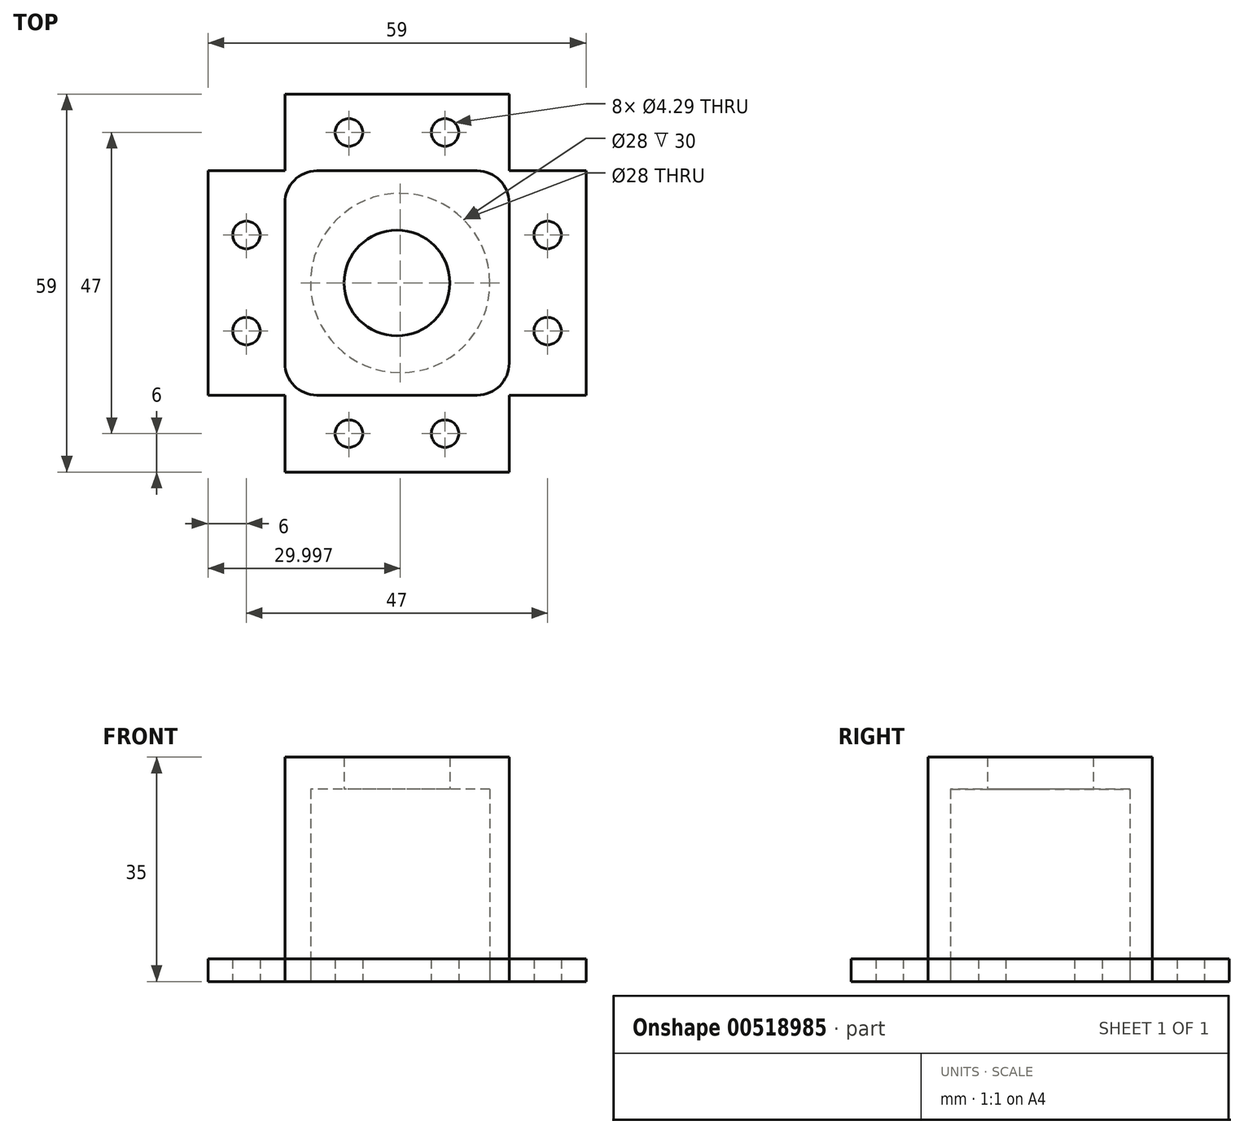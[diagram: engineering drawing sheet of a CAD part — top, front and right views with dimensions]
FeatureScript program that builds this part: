
annotation { "Feature Type Name" : "Feature", "Feature Type Description" : "" }
export const myFeature = defineFeature(function(context is Context, id is Id, definition is map)
    precondition{}
    {
        {
            var Q0;
            Q0=qCreatedBy(makeId("Top.planeOp"),FACE);
            var sketch = newSketch(context, id + "F0", { "sketchPlane" : qUnion([Q0])});
            skLineSegment(sketch, "E0.bottom", {"start": v(-17.5, 17.5) * mm, "end": v(17.5, 17.5) * mm});
            skLineSegment(sketch, "E0.top", {"start": v(-17.5, -17.5) * mm, "end": v(17.5, -17.5) * mm});
            skLineSegment(sketch, "E0.left", {"start": v(-17.5, 17.5) * mm, "end": v(-17.5, -17.5) * mm});
            skLineSegment(sketch, "E0.right", {"start": v(17.5, 17.5) * mm, "end": v(17.5, -17.5) * mm});
            skLineSegment(sketch, "E1.bottom", {"start": v(-17.5, 17.5) * mm, "end": v(-29.5, 17.5) * mm});
            skLineSegment(sketch, "E1.top", {"start": v(-17.5, -17.5) * mm, "end": v(-29.5, -17.5) * mm});
            skLineSegment(sketch, "E1.right", {"start": v(-29.5, 17.5) * mm, "end": v(-29.5, -17.5) * mm});
            skLineSegment(sketch, "E2.left", {"start": v(-17.5, 17.5) * mm, "end": v(-17.5, 17.5) * mm});
            skLineSegment(sketch, "E2.right", {"start": v(17.5, 17.5) * mm, "end": v(17.5, 17.5) * mm});
            skLineSegment(sketch, "E3.top", {"start": v(-17.5, 29.5) * mm, "end": v(17.5, 29.5) * mm});
            skLineSegment(sketch, "E3.left", {"start": v(-17.5, 17.5) * mm, "end": v(-17.5, 29.5) * mm});
            skLineSegment(sketch, "E3.right", {"start": v(17.5, 17.5) * mm, "end": v(17.5, 29.5) * mm});
            skLineSegment(sketch, "E4.bottom", {"start": v(17.5, 17.5) * mm, "end": v(29.5, 17.5) * mm});
            skLineSegment(sketch, "E4.top", {"start": v(17.5, -17.5) * mm, "end": v(29.5, -17.5) * mm});
            skLineSegment(sketch, "E4.right", {"start": v(29.5, 17.5) * mm, "end": v(29.5, -17.5) * mm});
            skLineSegment(sketch, "E5.top", {"start": v(-17.5, -29.5) * mm, "end": v(17.5, -29.5) * mm});
            skLineSegment(sketch, "E5.left", {"start": v(-17.5, -17.5) * mm, "end": v(-17.5, -29.5) * mm});
            skLineSegment(sketch, "E5.right", {"start": v(17.5, -17.5) * mm, "end": v(17.5, -29.5) * mm});
            skLineSegment(sketch, "E6", {"start": v(17.5, 17.5) * mm, "end": v(-17.5, -17.5) * mm, "construction": true});
            skLineSegment(sketch, "E7", {"start": v(-17.5, 17.5) * mm, "end": v(17.5, -17.5) * mm, "construction": true});
            skCircle(sketch, "E8", {"center": v(0, 0) * mm, "radius": 8.25 * mm});
            skCircle(sketch, "E9", {"center": v(-23.5, 7.5) * mm, "radius": 2.14 * mm});
            skCircle(sketch, "E10", {"center": v(-23.5, -7.5) * mm, "radius": 2.14 * mm});
            skCircle(sketch, "E11", {"center": v(23.5, -7.5) * mm, "radius": 2.14 * mm});
            skCircle(sketch, "E12", {"center": v(23.5, 7.5) * mm, "radius": 2.14 * mm});
            skCircle(sketch, "E13", {"center": v(-7.5, 23.5) * mm, "radius": 2.14 * mm});
            skCircle(sketch, "E14", {"center": v(7.5, 23.5) * mm, "radius": 2.14 * mm});
            skCircle(sketch, "E15", {"center": v(-7.5, -23.5) * mm, "radius": 2.14 * mm});
            skCircle(sketch, "E16", {"center": v(7.5, -23.5) * mm, "radius": 2.14 * mm});
            skLineSegment(sketch, "E17", {"start": v(-23.5, 7.5) * mm, "end": v(-29.5, 7.5) * mm, "construction": true});
            skLineSegment(sketch, "E18", {"start": v(-23.5, 7.5) * mm, "end": v(-17.5, 7.5) * mm, "construction": true});
            skLineSegment(sketch, "E19", {"start": v(23.5, -7.5) * mm, "end": v(29.5, -7.5) * mm, "construction": true});
            skLineSegment(sketch, "E20", {"start": v(23.5, -7.5) * mm, "end": v(17.5, -7.5) * mm, "construction": true});
            skLineSegment(sketch, "E21", {"start": v(7.5, -23.5) * mm, "end": v(7.5, -17.5) * mm, "construction": true});
            skLineSegment(sketch, "E22", {"start": v(7.5, -23.5) * mm, "end": v(7.5, -29.5) * mm, "construction": true});
            skLineSegment(sketch, "E23", {"start": v(7.5, 23.5) * mm, "end": v(7.5, 17.5) * mm, "construction": true});
            skLineSegment(sketch, "E24", {"start": v(7.5, 23.5) * mm, "end": v(7.5, 29.5) * mm, "construction": true});
            skLineSegment(sketch, "E25", {"start": v(7.5, 23.5) * mm, "end": v(17.5, 23.5) * mm, "construction": true});
            skLineSegment(sketch, "E26", {"start": v(-7.5, 23.5) * mm, "end": v(-17.5, 23.5) * mm, "construction": true});
            skLineSegment(sketch, "E27", {"start": v(-23.5, 7.5) * mm, "end": v(-23.5, 17.5) * mm, "construction": true});
            skLineSegment(sketch, "E28", {"start": v(-23.5, -7.5) * mm, "end": v(-23.5, -17.5) * mm, "construction": true});
            skSolve(sketch);
        }
        {
            var Q0;
            Q0=makeQuery(id+"F0.imprint","IMPRINT",FACE,{"disambiguationData":[TD([[makeQuery(id+"F0.imprint","IMPRINT",EDGE,{"derivedFrom":sQuery(id+"F0.wireOp",EDGE,"E1.bottom")}),1.0]])]});
            var Q1;
            Q1=makeQuery(id+"F0.imprint","IMPRINT",FACE,{"disambiguationData":[TD([[makeQuery(id+"F0.imprint","IMPRINT",EDGE,{"derivedFrom":sQuery(id+"F0.wireOp",EDGE,"E0.bottom")}),1.0]])]});
            var Q2;
            Q2=makeQuery(id+"F0.imprint","IMPRINT",FACE,{"disambiguationData":[TD([[makeQuery(id+"F0.imprint","IMPRINT",EDGE,{"derivedFrom":sQuery(id+"F0.wireOp",EDGE,"E4.bottom")}),-1.0]])]});
            var Q3;
            Q3=makeQuery(id+"F0.imprint","IMPRINT",FACE,{"disambiguationData":[TD([[makeQuery(id+"F0.imprint","IMPRINT",EDGE,{"derivedFrom":sQuery(id+"F0.wireOp",EDGE,"E0.top")}),-1.0]])]});
            var Q4;
            Q4=makeQuery(id+"F0.imprint","IMPRINT",FACE,{"disambiguationData":[TD([[makeQuery(id+"F0.imprint","IMPRINT",EDGE,{"derivedFrom":sQuery(id+"F0.wireOp",EDGE,"E0.left")}),1.0]])]});
            extrude(context, id + "F1", {"entities" : qUnion([Q0, Q1, Q2, Q3, Q4]), "depth" : 3.5 * mm, "offsetDistance" : 25 * mm});
        }
        {
            var Q0;
            Q0=makeQuery(id+"F0.imprint","IMPRINT",FACE,{"disambiguationData":[TD([[makeQuery(id+"F0.imprint","IMPRINT",EDGE,{"derivedFrom":sQuery(id+"F0.wireOp",EDGE,"E0.left")}),1.0]])]});
            extrude(context, id + "F2", {"entities" : qUnion([Q0]), "depth" : 35 * mm, "offsetDistance" : 25 * mm});
        }
        {
            var Q0;
            Q0=makeQuery(id+"F2.opExtrude","SWEPT_EDGE",EDGE,{"disambiguationData":[OSD([sQuery(id+"F0.wireOp",EDGE,"E1.top"),sQuery(id+"F0.wireOp",EDGE,"E0.left"),sQuery(id+"F0.wireOp",EDGE,"E0.top"),sQuery(id+"F0.wireOp",EDGE,"E5.left")])]});
            var Q1;
            Q1=makeQuery(id+"F2.opExtrude","SWEPT_EDGE",EDGE,{"disambiguationData":[OSD([sQuery(id+"F0.wireOp",EDGE,"E4.top"),sQuery(id+"F0.wireOp",EDGE,"E0.right"),sQuery(id+"F0.wireOp",EDGE,"E0.top"),sQuery(id+"F0.wireOp",EDGE,"E5.right")])]});
            var Q2;
            Q2=makeQuery(id+"F2.opExtrude","SWEPT_EDGE",EDGE,{"disambiguationData":[OSD([sQuery(id+"F0.wireOp",EDGE,"E0.bottom"),sQuery(id+"F0.wireOp",EDGE,"E3.right"),sQuery(id+"F0.wireOp",EDGE,"E4.bottom"),sQuery(id+"F0.wireOp",EDGE,"E0.right")])]});
            var Q3;
            Q3=makeQuery(id+"F2.opExtrude","SWEPT_EDGE",EDGE,{"disambiguationData":[OSD([sQuery(id+"F0.wireOp",EDGE,"E1.bottom"),sQuery(id+"F0.wireOp",EDGE,"E0.left"),sQuery(id+"F0.wireOp",EDGE,"E0.bottom"),sQuery(id+"F0.wireOp",EDGE,"E3.left")])]});
            fillet(context, id + "F3", {"entities" : qUnion([Q0, Q1, Q2, Q3]), "radius" : 5 * mm, "tangentPropagation" : true, "allowEdgeOverflow" : false});
        }
        {
            var Q0;
            Q0=makeQuery(id+"F0.imprint","IMPRINT",FACE,{"disambiguationData":[TD([[makeQuery(id+"F0.imprint","IMPRINT",EDGE,{"derivedFrom":sQuery(id+"F0.wireOp",EDGE,"E0.left")}),1.0]])]});
            var sketch = newSketch(context, id + "F4", { "sketchPlane" : qUnion([Q0])});
            skCircle(sketch, "E29", {"center": v(0.5, 0) * mm, "radius": 14 * mm});
            skSolve(sketch);
        }
        {
            var Q0;
            Q0 = qSketchRegion(id + "F4", true);
            extrude(context, id + "F5", {"entities" : qUnion([Q0]), "operationType" : NewBodyOperationType.REMOVE, "depth" : 30 * mm, "offsetDistance" : 25 * mm});
        }
    });
